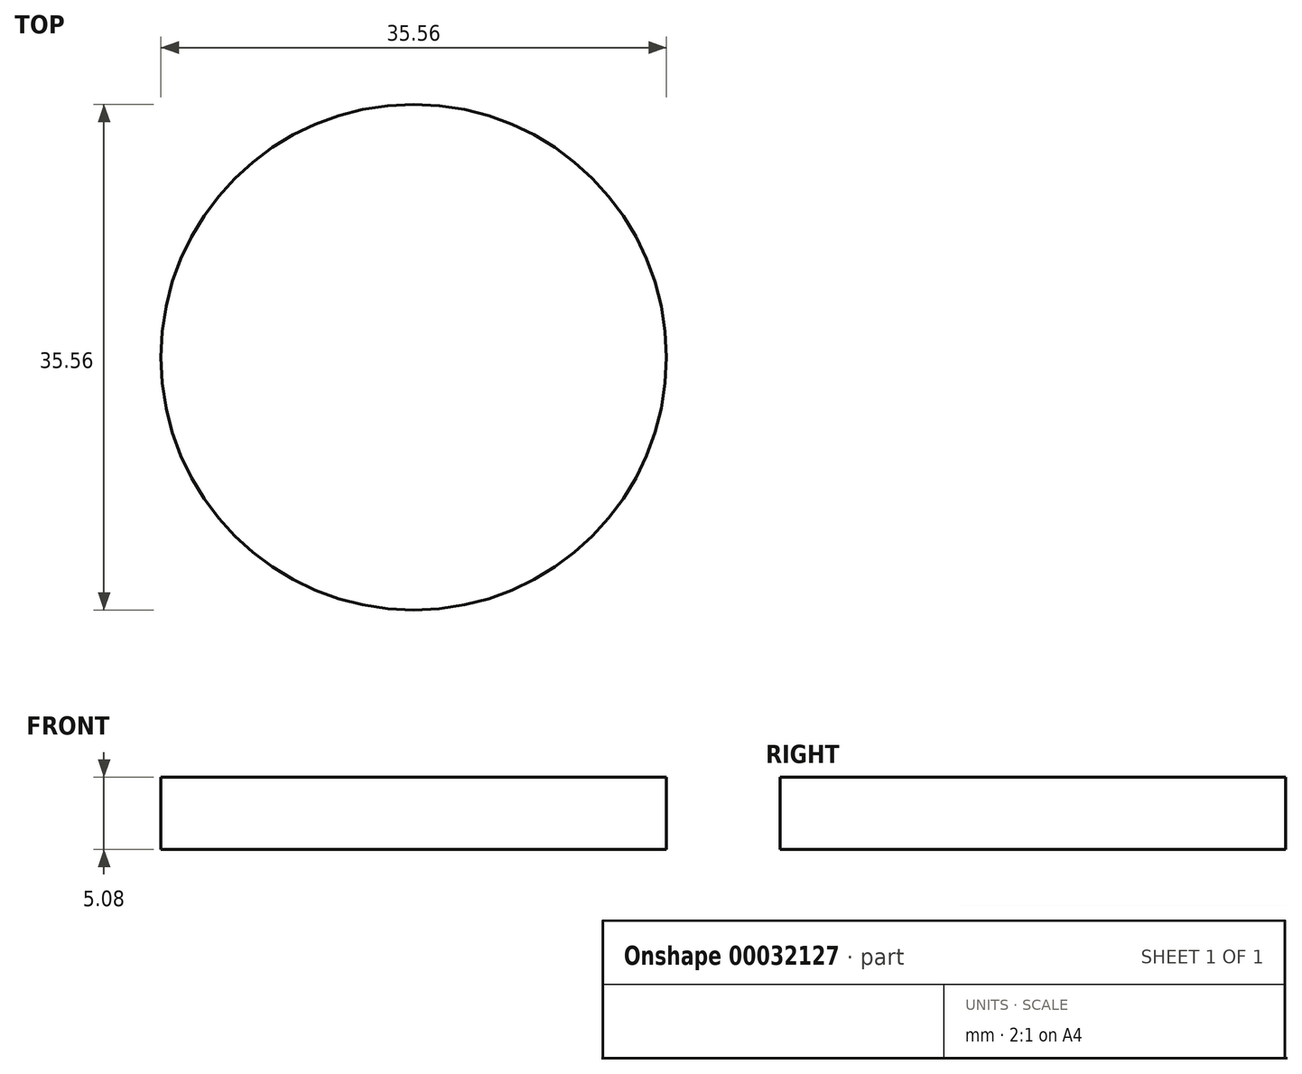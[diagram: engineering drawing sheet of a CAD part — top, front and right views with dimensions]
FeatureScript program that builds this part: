
annotation { "Feature Type Name" : "Feature", "Feature Type Description" : "" }
export const myFeature = defineFeature(function(context is Context, id is Id, definition is map)
    precondition{}
    {
        {
            var Q0;
            Q0=qCreatedBy(makeId("Top.planeOp"),FACE);
            var sketch = newSketch(context, id + "F0", { "sketchPlane" : qUnion([Q0])});
            skCircle(sketch, "E0", {"center": v(0, 0) * mm, "radius": 17.78 * mm});
            skSolve(sketch);
        }
        {
            var Q0;
            Q0 = qSketchRegion(id + "F0", true);
            extrude(context, id + "F1", {"entities" : qUnion([Q0]), "depth" : 5.08 * mm});
        }
    });
